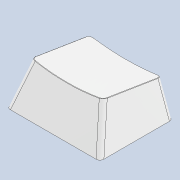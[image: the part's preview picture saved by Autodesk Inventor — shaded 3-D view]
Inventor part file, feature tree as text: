
AUTODESK INVENTOR PART (.ipt)
format: ipt  version: 2021 (Build 250183000, 183)  size: 250,880 bytes
history: native  units: in
note: dims shown in document units (in); Inventor stores cm internally (conversion verified against a paired STEP export)
features: chamfer x1
ambient origin geometry x8: Origin, YZ Plane, XZ Plane, XY Plane, X Axis, Y Axis, Z Axis, Center Point
bodies: Solid1 (feature_tree)
feature tree (1):
  chamfer  "Chamfer1"  [1 undecoded]
note: 1 required parameter value undecoded (feature->parameter linkage not recoverable at this tier; creation-order binding heuristic only, values carry confidence <= 0.55)
